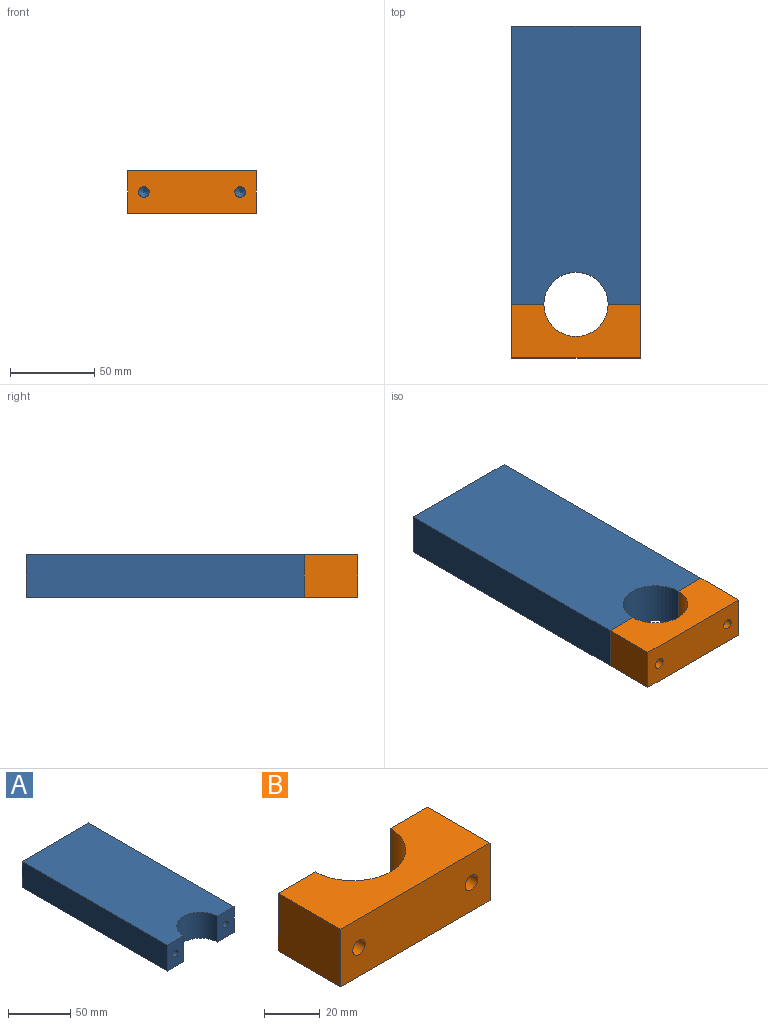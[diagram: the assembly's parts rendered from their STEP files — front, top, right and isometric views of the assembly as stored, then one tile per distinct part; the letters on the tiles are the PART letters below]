
ASSEMBLY  parts=2 mates=1
PART A: 12 faces, bbox 76.2x165.1x25.4 mm
  f0: plane 165.1x25.4mm, normal (1,0,0), area 4193.5mm2, adj f1,f5,f6,f7
  f1: plane 76.2x25.4mm, normal (0,1,0), area 1935.5mm2, adj f0,f2,f6,f7
  f2: plane 165.1x25.4mm, normal (-1,0,0), area 4193.5mm2, adj f1,f3,f6,f7
  f3: plane 25.4x19.05mm, normal (0,-1,0), area 452.2mm2, adj f2,f4,f6,f7,f11
  f4: cylinder r=19.05mm len=38.1mm, axis (0,0,-1), area 1520.1mm2, adj f3,f5,f6,f7
  f5: plane 25.4x19.05mm, normal (0,-1,0), area 452.2mm2, adj f0,f4,f6,f7,f9
  f6: plane 165.1x76.2mm, normal (0,0,1), area 12010.6mm2, adj f0,f1,f2,f3,f4,f5
  f7: plane 165.1x76.2mm, normal (0,0,-1), area 12010.6mm2, adj f0,f1,f2,f3,f4,f5
  f8: cone r=0mm half-angle=59deg, axis (0,-1,0), area 36.9mm2, adj f9
  f9: cylinder r=3.17mm len=19.05mm, axis (0,-1,0), area 380mm2, adj f5,f8
  f10: cone r=0mm half-angle=59deg, axis (0,-1,0), area 36.9mm2, adj f11
  f11: cylinder r=3.17mm len=19.05mm, axis (0,-1,0), area 380mm2, adj f3,f10
PART B: 10 faces, bbox 76.2x31.8x25.4 mm
  f0: plane 25.4x19.05mm, normal (0,1,0), area 452.2mm2, adj f1,f5,f6,f7,f9
  f1: plane 31.75x25.4mm, normal (-1,0,0), area 806.5mm2, adj f0,f2,f6,f7
  f2: plane 76.2x25.4mm, normal (0,-1,0), area 1872.1mm2, adj f1,f3,f6,f7,f8,f9
  f3: plane 31.75x25.4mm, normal (1,0,0), area 806.5mm2, adj f2,f4,f6,f7
  f4: plane 25.4x19.05mm, normal (0,1,0), area 452.2mm2, adj f3,f5,f6,f7,f8
  f5: cylinder r=19.05mm len=38.1mm, axis (0,0,-1), area 1520.1mm2, adj f0,f4,f6,f7
  f6: plane 76.2x31.75mm, normal (0,0,1), area 1849.3mm2, adj f0,f1,f2,f3,f4,f5
  f7: plane 76.2x31.75mm, normal (0,0,-1), area 1849.3mm2, adj f0,f1,f2,f3,f4,f5
  f8: cylinder r=3.17mm len=31.75mm, axis (0,1,0), area 633.4mm2, adj f2,f4
  f9: cylinder r=3.17mm len=31.75mm, axis (0,1,0), area 633.4mm2, adj f0,f2
PLACE A t=(-74.16,-29.24,-14.22)mm
PLACE B rot(axis=(0,0,1),0deg) t=(-74.16,-194.34,-14.22)mm
MATE parallel B.f9 <-> A.f10  axis (0,1,0) through (-64.63,-194.34,-1.52)mm
